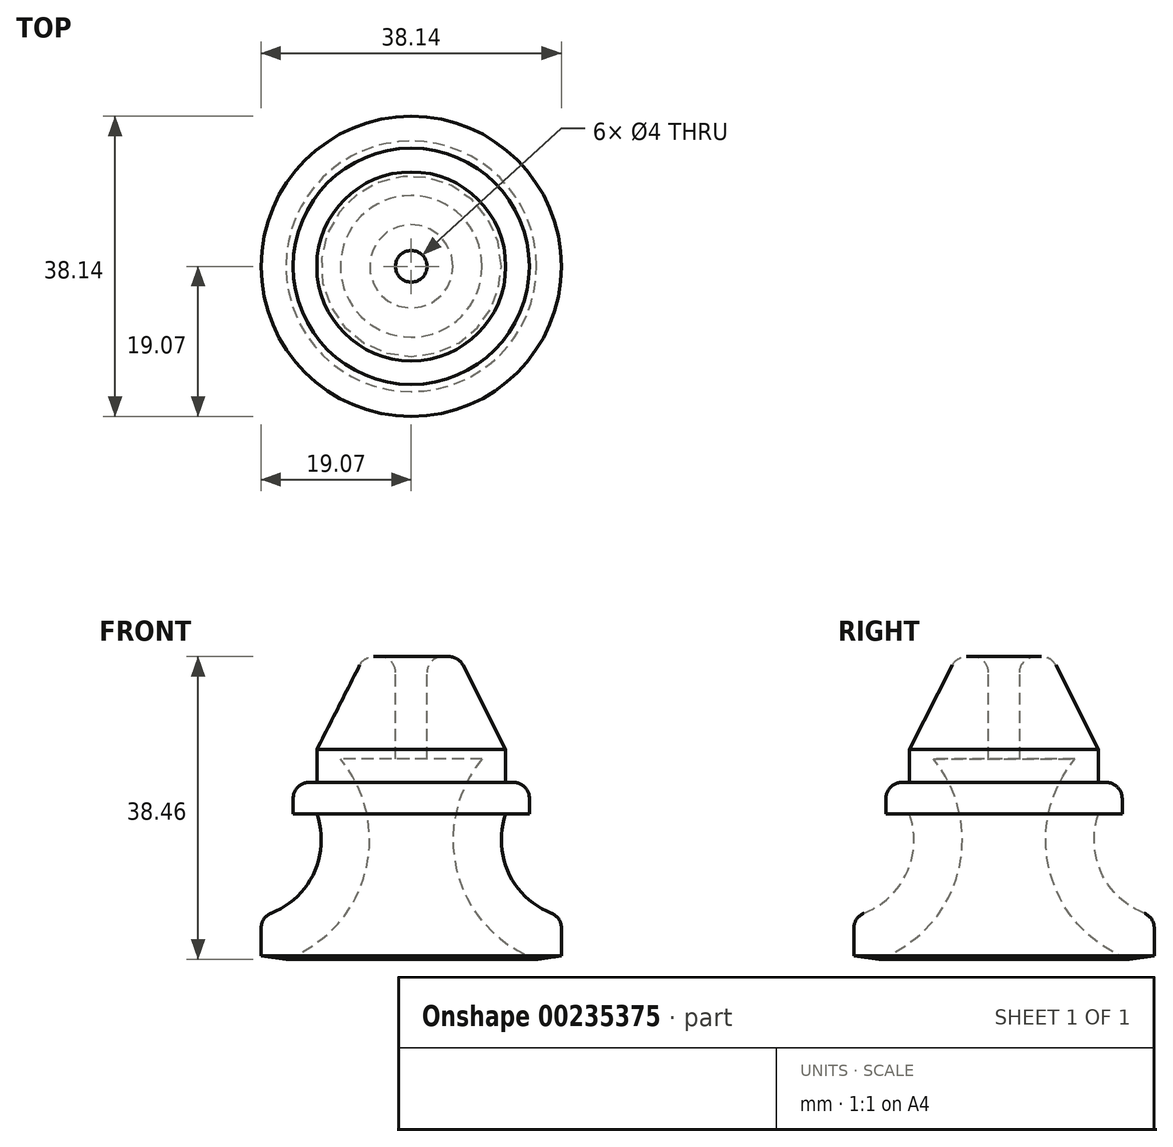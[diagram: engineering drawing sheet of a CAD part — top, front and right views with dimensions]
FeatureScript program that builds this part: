
annotation { "Feature Type Name" : "Feature", "Feature Type Description" : "" }
export const myFeature = defineFeature(function(context is Context, id is Id, definition is map)
    precondition{}
    {
        {
            var Q0;
            Q0=qCreatedBy(makeId("Front.planeOp"),FACE);
            var sketch = newSketch(context, id + "F0", { "sketchPlane" : qUnion([Q0])});
            skLineSegment(sketch, "E0", {"start": v(0, 28.61) * mm, "end": v(0, -13.7) * mm, "construction": true});
            skLineSegment(sketch, "E1", {"start": v(2, 23.29) * mm, "end": v(6, 23.29) * mm});
            skLineSegment(sketch, "E2", {"start": v(12, 7.29) * mm, "end": v(15, 7.29) * mm});
            skLineSegment(sketch, "E3", {"start": v(15, 7.29) * mm, "end": v(15, 3.29) * mm});
            skLineSegment(sketch, "E4", {"start": v(15, 3.29) * mm, "end": v(12, 3.29) * mm});
            skArc(sketch, "E5", {"start": v(12, 3.29) * mm, "mid": v(12.66, -4.78) * mm, "end": v(19.07, -9.71) * mm});
            skLineSegment(sketch, "E6", {"start": v(19.07, -9.71) * mm, "end": v(19.07, -14.71) * mm});
            skArc(sketch, "E7.0", {"start": v(9, 10.29) * mm, "mid": v(5.86, -4.23) * mm, "end": v(15.91, -15.17) * mm});
            skLineSegment(sketch, "E8", {"start": v(2, 23.29) * mm, "end": v(2, 10.29) * mm});
            skLineSegment(sketch, "E9", {"start": v(2, 10.29) * mm, "end": v(9, 10.29) * mm});
            skLineSegment(sketch, "E10", {"start": v(15.91, -15.17) * mm, "end": v(19.07, -14.71) * mm});
            skLineSegment(sketch, "E11", {"start": v(12, 7.29) * mm, "end": v(12, 11.47) * mm});
            skLineSegment(sketch, "E12", {"start": v(12, 11.47) * mm, "end": v(6, 23.29) * mm});
            skSolve(sketch);
        }
        {
            var Q0;
            Q0 = qSketchRegion(id + "F0", true);
            var Q1;
            Q1=sQuery(id+"F0.wireOp",EDGE,"E0");
            revolve(context, id + "F1", {"entities" : qUnion([Q0]), "axis" : qUnion([Q1]), "revolveType" : RevolveType.FULL});
        }
        {
            var Q0;
            Q0=makeQuery(id+"F1.opRevolve","SWEPT_EDGE",EDGE,{"disambiguationData":[OSD([sQuery(id+"F0.wireOp",EDGE,"E1"),sQuery(id+"F0.wireOp",EDGE,"ydA1G0gd-u6Pf-Ut2F-UHt6-uX8tDONLldMU")])]});
            var Q1;
            Q1=makeQuery(id+"F1.opRevolve","SWEPT_EDGE",EDGE,{"disambiguationData":[OSD([sQuery(id+"F0.wireOp",EDGE,"E2"),sQuery(id+"F0.wireOp",EDGE,"E3")])]});
            var Q2;
            Q2=makeQuery(id+"F1.opRevolve","SWEPT_EDGE",EDGE,{"disambiguationData":[OSD([sQuery(id+"F0.wireOp",EDGE,"E5"),sQuery(id+"F0.wireOp",EDGE,"E6")])]});
            fillet(context, id + "F2", {"entities" : qUnion([Q0, Q1, Q2]), "radius" : 2 * mm, "tangentPropagation" : true, "allowEdgeOverflow" : false});
        }
    });
